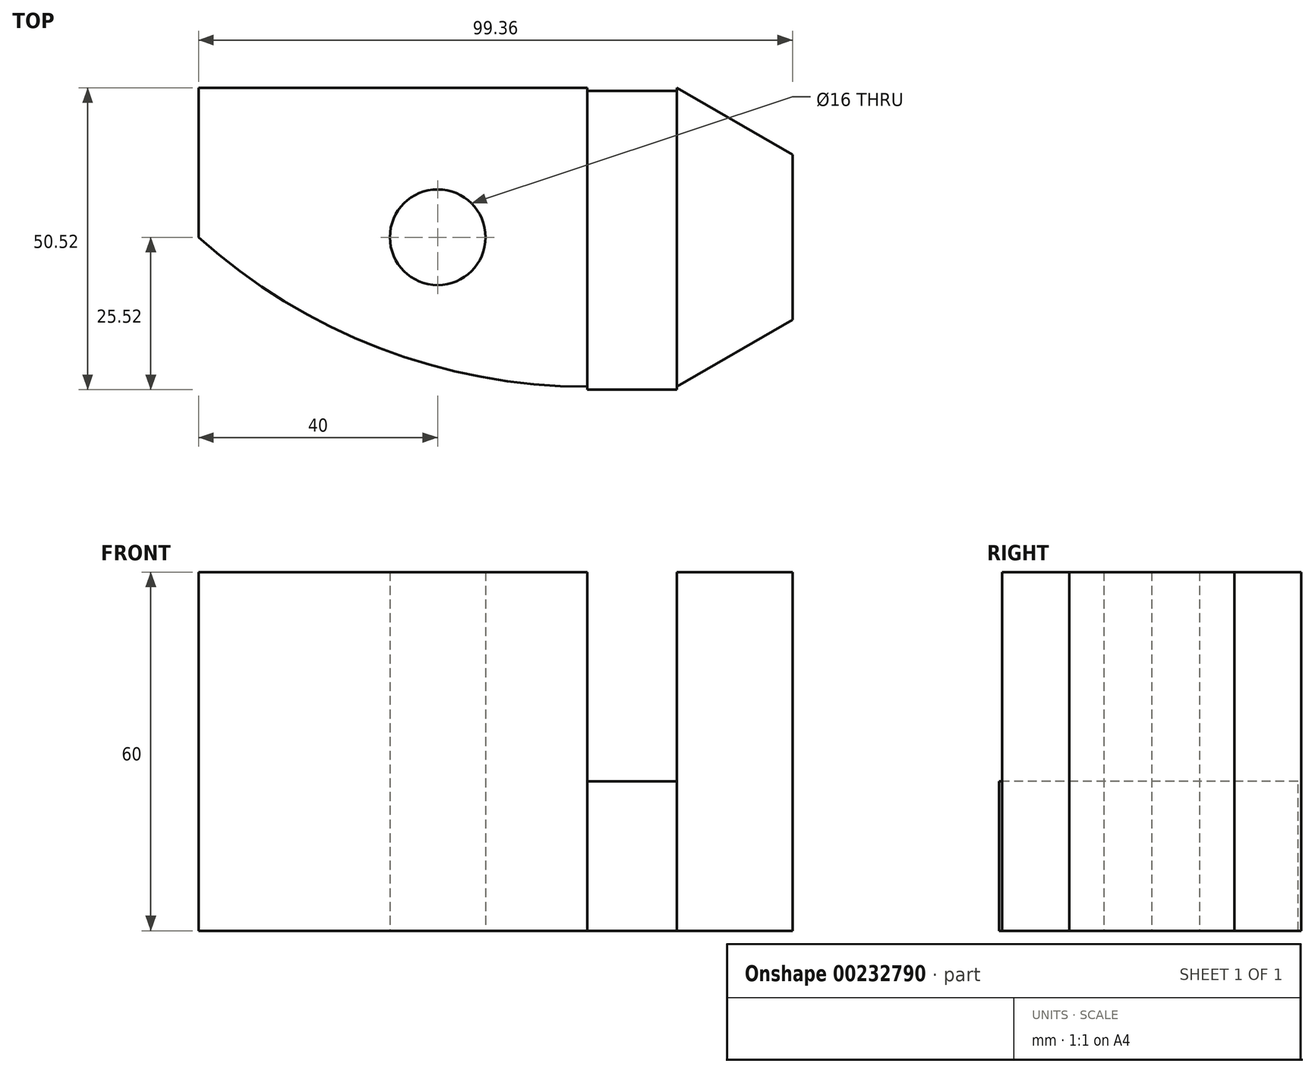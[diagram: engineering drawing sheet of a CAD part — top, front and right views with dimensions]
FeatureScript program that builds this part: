
annotation { "Feature Type Name" : "Feature", "Feature Type Description" : "" }
export const myFeature = defineFeature(function(context is Context, id is Id, definition is map)
    precondition{}
    {
        {
            var Q0;
            Q0=qCreatedBy(makeId("Top.planeOp"),FACE);
            var sketch = newSketch(context, id + "F0", { "sketchPlane" : qUnion([Q0])});
            skArc(sketch, "E0", {"start": v(-65, -25) * mm, "mid": v(-34.82, -43.53) * mm, "end": v(0, -50) * mm});
            skLineSegment(sketch, "E1", {"start": v(-65, 0) * mm, "end": v(-65, -25) * mm});
            skLineSegment(sketch, "E2", {"start": v(-65, -25) * mm, "end": v(0, -25) * mm});
            skLineSegment(sketch, "E3", {"start": v(0, -25) * mm, "end": v(0, -50) * mm});
            skLineSegment(sketch, "E4", {"start": v(-65, 0) * mm, "end": v(0, 0) * mm});
            skLineSegment(sketch, "E5", {"start": v(0, -25) * mm, "end": v(0, 0) * mm});
            skLineSegment(sketch, "E6", {"start": v(0, -50) * mm, "end": v(0, -25) * mm});
            skLineSegment(sketch, "E7", {"start": v(0, 0) * mm, "end": v(-65, 0) * mm});
            skSolve(sketch);
        }
        {
            var Q0;
            Q0=qCreatedBy(makeId("Top.planeOp"),FACE);
            var sketch = newSketch(context, id + "F1", { "sketchPlane" : qUnion([Q0])});
            skLineSegment(sketch, "E8", {"start": v(0, -50) * mm, "end": v(15, -50) * mm});
            skLineSegment(sketch, "E9", {"start": v(15, -50) * mm, "end": v(15, 0) * mm});
            skLineSegment(sketch, "E10", {"start": v(15, 0) * mm, "end": v(0, 0) * mm});
            skLineSegment(sketch, "E11", {"start": v(34.36, -38.82) * mm, "end": v(34.36, -11.18) * mm});
            skLineSegment(sketch, "E12", {"start": v(15, 0) * mm, "end": v(34.36, -11.18) * mm});
            skLineSegment(sketch, "E13", {"start": v(15, -50) * mm, "end": v(34.36, -38.82) * mm});
            skCircle(sketch, "E14", {"center": v(-25, -25) * mm, "radius": 8 * mm});
            skLineSegment(sketch, "E15", {"start": v(15, -50) * mm, "end": v(0, -50) * mm});
            skLineSegment(sketch, "E16", {"start": v(32.47, -5.17) * mm, "end": v(47.47, -5.17) * mm});
            skLineSegment(sketch, "E17", {"start": v(47.47, -5.17) * mm, "end": v(47.47, 44.83) * mm});
            skLineSegment(sketch, "E18", {"start": v(47.47, 44.83) * mm, "end": v(32.47, 44.83) * mm});
            skLineSegment(sketch, "E19", {"start": v(66.83, 6) * mm, "end": v(66.83, 33.65) * mm});
            skLineSegment(sketch, "E20", {"start": v(47.47, 44.83) * mm, "end": v(66.83, 33.65) * mm});
            skLineSegment(sketch, "E21", {"start": v(47.47, -5.17) * mm, "end": v(66.83, 6) * mm});
            skCircle(sketch, "E22", {"center": v(7.47, 19.83) * mm, "radius": 8 * mm});
            skLineSegment(sketch, "E23", {"start": v(47.47, -5.17) * mm, "end": v(32.47, -5.17) * mm});
            skSolve(sketch);
        }
        {
            var Q0;
            Q0=makeQuery(id+"F1.imprint","IMPRINT",FACE,{"disambiguationData":[TD([[makeQuery(id+"F1.imprint","IMPRINT",EDGE,{"derivedFrom":sQuery(id+"F1.wireOp",EDGE,"E14")}),1.0]])]});
            var sketch = newSketch(context, id + "F2", { "sketchPlane" : qUnion([Q0])});
            skSolve(sketch);
        }
        {
            var Q0;
            Q0=makeQuery(id+"F0.imprint","IMPRINT",FACE,{"disambiguationData":[TD([[makeQuery(id+"F0.imprint","IMPRINT",EDGE,{"derivedFrom":sQuery(id+"F0.wireOp",EDGE,"E0")}),1.0]])]});
            var Q1;
            Q1=makeQuery(id+"F0.imprint","IMPRINT",FACE,{"disambiguationData":[TD([[makeQuery(id+"F0.imprint","IMPRINT",EDGE,{"derivedFrom":sQuery(id+"F0.wireOp",EDGE,"E1")}),1.0]])]});
            var Q2;
            Q2=makeQuery(id+"F1.imprint","IMPRINT",FACE,{"disambiguationData":[TD([[makeQuery(id+"F1.imprint","IMPRINT",EDGE,{"derivedFrom":sQuery(id+"F1.wireOp",EDGE,"E9")}),-1.0]])]});
            extrude(context, id + "F3", {"entities" : qUnion([Q0, Q1, Q2]), "depth" : 60 * mm});
        }
        {
            var Q0;
            Q0=makeQuery(id+"F2.imprint","IMPRINT",FACE,{"disambiguationData":[TD([[makeQuery(id+"F2.imprint","IMPRINT",EDGE,{"derivedFrom":makeQuery(id+"F1.imprint","IMPRINT",EDGE,{"derivedFrom":sQuery(id+"F1.wireOp",EDGE,"E14")})}),1.0]])]});
            extrude(context, id + "F4", {"entities" : qUnion([Q0]), "operationType" : NewBodyOperationType.REMOVE, "depth" : 60 * mm});
        }
        {
            var Q0;
            Q0=qCreatedBy(makeId("Top.planeOp"),FACE);
            var sketch = newSketch(context, id + "F5", { "sketchPlane" : qUnion([Q0])});
            skLineSegment(sketch, "E24", {"start": v(0, -50.52) * mm, "end": v(15, -50.52) * mm});
            skLineSegment(sketch, "E25", {"start": v(0, 0) * mm, "end": v(15, 0) * mm});
            skSolve(sketch);
        }
        {
            var Q0;
            Q0=sQuery(id+"F5.wireOp",EDGE,"E24");
            var Q1;
            Q1=sQuery(id+"F5.wireOp",EDGE,"E25");
            extrude(context, id + "F6", {"bodyType" : ToolBodyType.SURFACE, "surfaceEntities" : qUnion([Q0, Q1]), "depth" : 25 * mm});
        }
        {
            var Q0;
            Q0=makeQuery(id+"F6.opExtrude","SWEPT_FACE",FACE,{"disambiguationData":[OSD([sQuery(id+"F5.wireOp",EDGE,"E24")])]});
            extrude(context, id + "F7", {"entities" : qUnion([Q0]), "oppositeDirection" : true, "depth" : 50 * mm});
        }
    });
